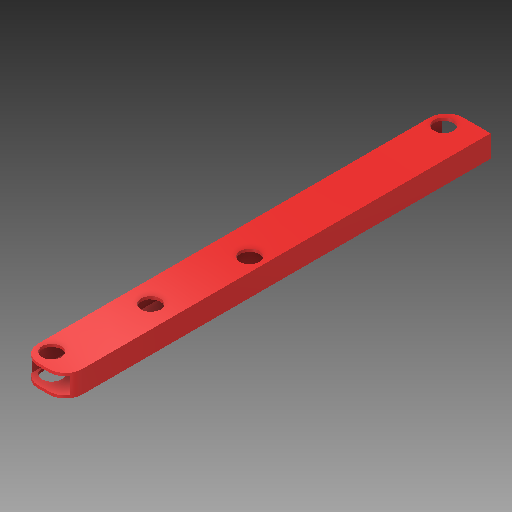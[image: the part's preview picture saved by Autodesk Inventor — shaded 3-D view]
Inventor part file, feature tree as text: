
AUTODESK INVENTOR PART (.ipt)
format: ipt  version: 2017 SP1 (Build 210196100, 196)  size: 143,360 bytes
history: native  units: in
note: dims shown in document units (in); Inventor stores cm internally (conversion verified against a paired STEP export)
features: extrude x2, sketch x2, fillet x1
ambient origin geometry x8: Origin, YZ Plane, XZ Plane, XY Plane, X Axis, Y Axis, Z Axis, Center Point
bodies: Solid1 (feature_tree)
feature tree (5):
  extrude  "Extrusion1"  Depth=2.0in
  extrude  "Extrusion2"  Depth=19.25in TaperAngle=0.0deg
  fillet  "Fillet1"  Radius=0.875in
  sketch  "Sketch1"  dims[d0=1.0in d1=2.0in]
  sketch  "Sketch2"  dims[d2=0.125in d3=19.25in d4=0.0in d5=0.875in d7=8.25in d10=0.875in d11=20.0in d12=0.0in d13=0.75in d16=0.75in d17=0.625in d20=0.75in d21=0.625in d23=0.625in]
